# Revit family: DDW24M999U_Revit
name_source: partatom
category: Specialty Equipment
revit_build: Autodesk Revit MEP 2014 (Build: 20130308_1515(x64)
units: mm (PartAtom-declared; Revit-internal decimal feet)

## types (1)
- DDW24M999U
    Adjustable Height = Yes
    Adjustable Tines = Yes
    Annual Consumption (kWh/yr) = 239
    Auto = Yes
    Auto Door Open - AutoRelease = Yes
    Basket Handle = Yes
    Cancel and Drain Button = Yes
    Capacity (Place Settings) = 14
    Capacity - 14 Place Settings = Yes
    Circuit Breaker (A) = 15
    Control Lock = Yes
    Cutlery Basket = Yes
    Cutlery Tray = Yes
    Cydle Time (min) - Normal Cycle = 114-150
    Delay Start = Yes (1-24 Hrs)
    Delicate = Yes
    Depth = 22 3/4"
    Description = 24-INCH DISHWASHER MODERNIST COLLECTION
    Display = Glass, Frosted
    Display Light Color = White
    Door = Stainless Steel
    Energy Source = Electric
    Energy Star Certified = Yes
    Express 60 = Yes
    FINISH = STAINLESS STEEL
    Fold Down Tines = Yes
    Foldable Cup Shelves = Yes
    Frequency (Hz) = 60
    Half Load = Yes
    Heater Position = Hidden
    Heater Watts = 1100
    Heavy = Yes
    Height = 32 1/4"
    Hi-Temp Wash = Yes
    Hidden Touch = Yes
    Leakage Sensor = Yes
    Manufacturer = Dacor
    Maximum Dish Size = 12”
    Model = DDW24M999U
    Noise Level (dBA) = 42
    Normal = Yes
    Rinse Only = Yes
    Sanitize = Yes
    Self Clean = Yes
    Smart Control (Wi-Fi) = Yes
    Speed Booster = Yes
    Time Remaining Indicator = Yes
    Total Options = 8
    Total Programs = 7
    Tub Material = Stainless Steel
    Unit = Plastic-Black
    Volts (V) = 120
    Water Consumption (gallons/cycle) = 3.2
    WaterWall™ = Yes
    Wide Pocket Handle = Yes
    Width = 23 1/2"
    Zone Booster = Yes

## geometry (parser evidence)
native form markers: Sweep x1
no freeform markers — native parametric forms only
